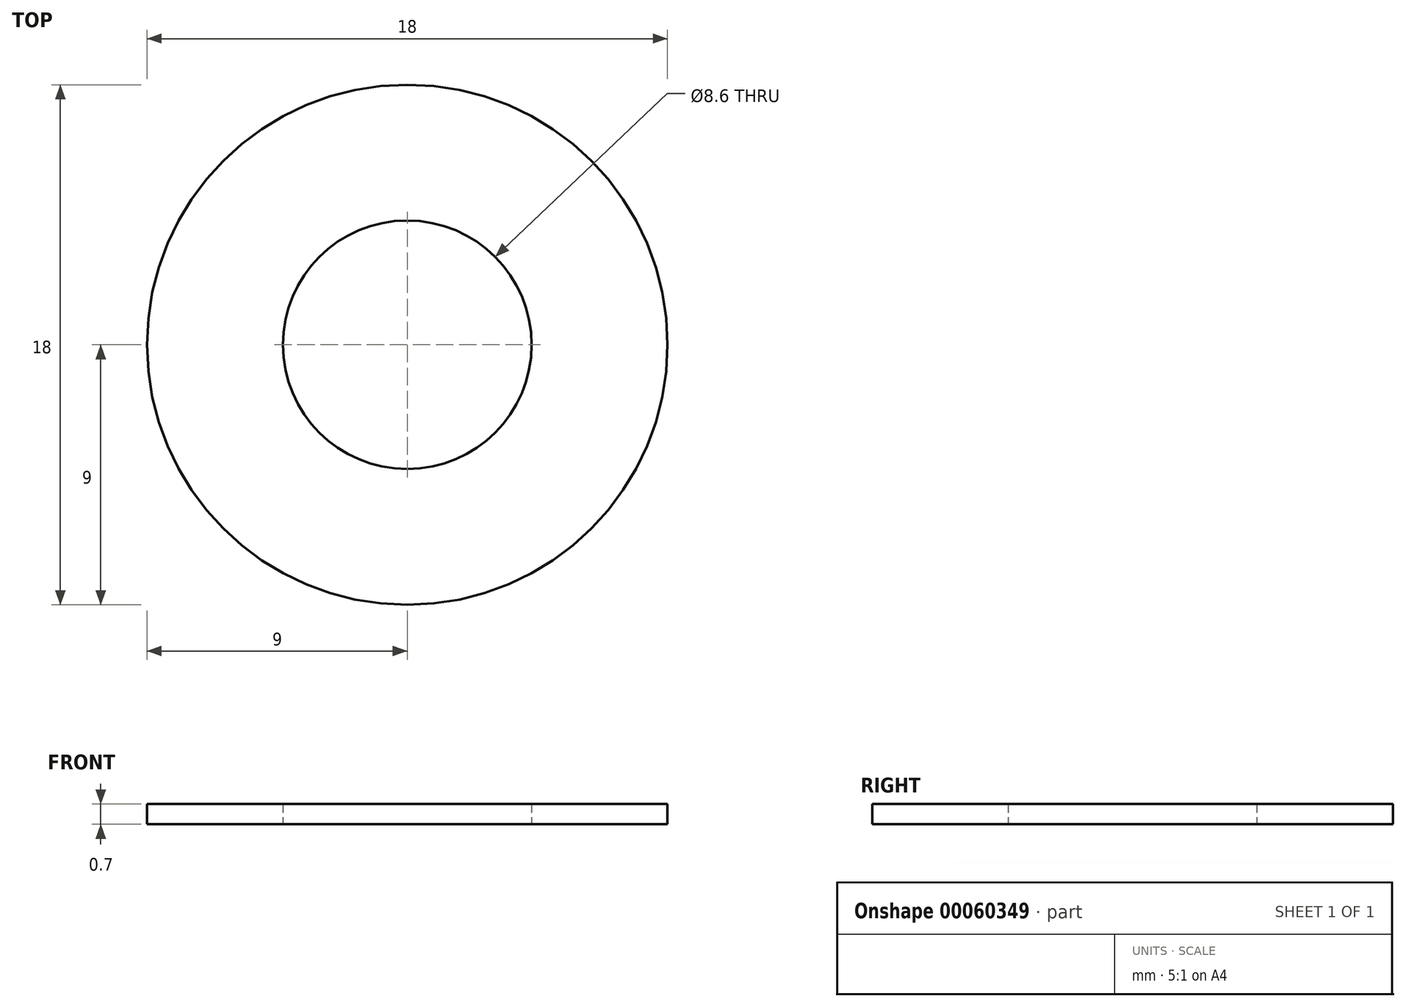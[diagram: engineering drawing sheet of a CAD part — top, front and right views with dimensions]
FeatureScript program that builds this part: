
annotation { "Feature Type Name" : "Feature", "Feature Type Description" : "" }
export const myFeature = defineFeature(function(context is Context, id is Id, definition is map)
    precondition{}
    {
        {
            var Q0;
            Q0=qCreatedBy(makeId("Front.planeOp"),FACE);
            var sketch = newSketch(context, id + "F0", { "sketchPlane" : qUnion([Q0])});
            skLineSegment(sketch, "E0.bottom", {"start": v(9, 0.7) * mm, "end": v(4.3, 0.7) * mm});
            skLineSegment(sketch, "E0.top", {"start": v(9, 0) * mm, "end": v(4.3, 0) * mm});
            skLineSegment(sketch, "E0.left", {"start": v(9, 0.7) * mm, "end": v(9, 0) * mm});
            skLineSegment(sketch, "E0.right", {"start": v(4.3, 0.7) * mm, "end": v(4.3, 0) * mm});
            skLineSegment(sketch, "E1", {"start": v(0, 0) * mm, "end": v(0, 6.48) * mm, "construction": true});
            skLineSegment(sketch, "E2.MirrorCS", {"start": v(-9, 0.7) * mm, "end": v(-4.3, 0.7) * mm, "construction": true});
            skLineSegment(sketch, "E3.MirrorCS", {"start": v(-9, 0.7) * mm, "end": v(-9, 0) * mm, "construction": true});
            skLineSegment(sketch, "E4.MirrorCS", {"start": v(-9, 0) * mm, "end": v(-4.3, 0) * mm, "construction": true});
            skLineSegment(sketch, "E5.MirrorCS", {"start": v(-4.3, 0.7) * mm, "end": v(-4.3, 0) * mm, "construction": true});
            skSolve(sketch);
        }
        {
            var Q0;
            Q0=makeQuery(id+"F0.imprint","IMPRINT",FACE,{"disambiguationData":[TD([[makeQuery(id+"F0.imprint","IMPRINT",EDGE,{"derivedFrom":sQuery(id+"F0.wireOp",EDGE,"E0.bottom")}),1.0]])]});
            var Q1;
            Q1=sQuery(id+"F0.wireOp",EDGE,"E1");
            revolve(context, id + "F1", {"entities" : qUnion([Q0]), "axis" : qUnion([Q1]), "revolveType" : RevolveType.FULL});
        }
    });
